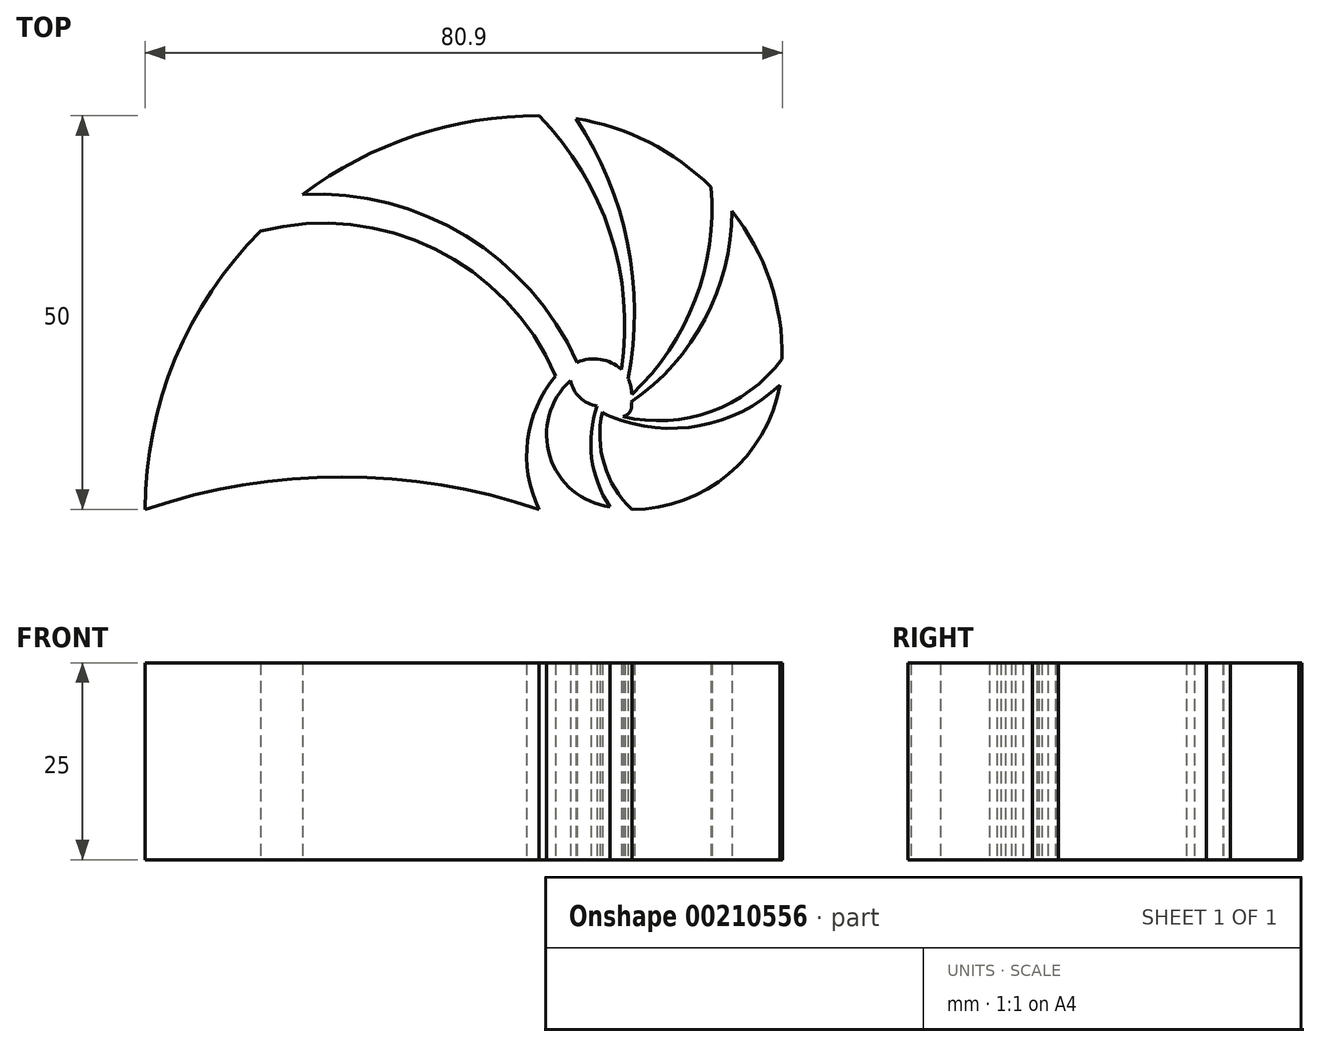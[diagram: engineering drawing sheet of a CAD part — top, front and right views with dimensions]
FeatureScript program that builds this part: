
annotation { "Feature Type Name" : "Feature", "Feature Type Description" : "" }
export const myFeature = defineFeature(function(context is Context, id is Id, definition is map)
    precondition{}
    {
        {
            var Q0;
            Q0=qCreatedBy(makeId("Top.planeOp"),FACE);
            var sketch = newSketch(context, id + "F0", { "sketchPlane" : qUnion([Q0])});
            skPoint(sketch, "E0", {"position": v(4.04, -30.8) * mm});
            skArc(sketch, "E1", {"start": v(-45.96, -30.8) * mm, "mid": v(-31.32, 4.55) * mm, "end": v(4.04, 19.2) * mm, "construction": true});
            skArc(sketch, "E2.MirrorCS", {"start": v(4.04, 19.2) * mm, "mid": v(25.89, 10.14) * mm, "end": v(34.94, -11.7) * mm, "construction": true});
            skArc(sketch, "E3.MirrorCS", {"start": v(34.94, -11.7) * mm, "mid": v(29.34, -25.21) * mm, "end": v(15.84, -30.8) * mm, "construction": true});
            skArc(sketch, "E4.MirrorCS", {"start": v(15.84, -30.8) * mm, "mid": v(7.5, -27.35) * mm, "end": v(4.05, -19) * mm, "construction": true});
            skArc(sketch, "E5.MirrorCS", {"start": v(4.04, -19) * mm, "mid": v(6.17, -13.85) * mm, "end": v(11.34, -11.7) * mm, "construction": true});
            skArc(sketch, "E6.MirrorCS", {"start": v(11.34, -11.7) * mm, "mid": v(14.52, -13.03) * mm, "end": v(15.84, -16.2) * mm, "construction": true});
            skPoint(sketch, "E7", {"position": v(-31.32, 4.55) * mm});
            skPoint(sketch, "E8", {"position": v(25.89, 10.14) * mm});
            skPoint(sketch, "E9", {"position": v(29.34, -25.21) * mm});
            skPoint(sketch, "E10", {"position": v(7.5, -27.35) * mm});
            skPoint(sketch, "E11", {"position": v(6.17, -13.85) * mm});
            skPoint(sketch, "E12", {"position": v(14.52, -13.03) * mm});
            skArc(sketch, "E13", {"start": v(-31.32, 4.55) * mm, "mid": v(-42.16, -11.67) * mm, "end": v(-45.96, -30.8) * mm});
            skArc(sketch, "E14", {"start": v(4.04, -30.8) * mm, "mid": v(-20.96, -26.69) * mm, "end": v(-45.96, -30.8) * mm});
            skArc(sketch, "E15", {"start": v(6.17, -13.85) * mm, "mid": v(-9.18, 2.27) * mm, "end": v(-31.32, 4.55) * mm});
            skArc(sketch, "E16", {"start": v(6.17, -13.85) * mm, "mid": v(2.6, -22.01) * mm, "end": v(4.04, -30.8) * mm});
            skArc(sketch, "E17", {"start": v(4.04, 19.2) * mm, "mid": v(-11.79, 16.67) * mm, "end": v(-25.96, 9.2) * mm});
            skArc(sketch, "E18", {"start": v(14.52, -13.03) * mm, "mid": v(11.83, -11.76) * mm, "end": v(8.88, -12.13) * mm});
            skArc(sketch, "E19", {"start": v(8.88, -12.13) * mm, "mid": v(-5.25, 3.9) * mm, "end": v(-25.96, 9.2) * mm});
            skArc(sketch, "E20", {"start": v(14.52, -13.03) * mm, "mid": v(13.08, 4.32) * mm, "end": v(4.04, 19.2) * mm});
            skArc(sketch, "E21", {"start": v(25.89, 10.14) * mm, "mid": v(18, 15.85) * mm, "end": v(8.73, 18.83) * mm});
            skArc(sketch, "E22", {"start": v(15.37, -14.22) * mm, "mid": v(15.3, 2.96) * mm, "end": v(8.73, 18.83) * mm});
            skArc(sketch, "E23", {"start": v(15.84, -16.2) * mm, "mid": v(23.88, -4.19) * mm, "end": v(25.89, 10.14) * mm});
            skArc(sketch, "E24", {"start": v(15.84, -16.2) * mm, "mid": v(15.7, -15.19) * mm, "end": v(15.37, -14.22) * mm});
            skArc(sketch, "E25", {"start": v(34.94, -11.7) * mm, "mid": v(33.39, -1.77) * mm, "end": v(28.58, 7.07) * mm});
            skArc(sketch, "E26", {"start": v(14.71, -19.02) * mm, "mid": v(15.64, -18.33) * mm, "end": v(15.75, -17.17) * mm});
            skArc(sketch, "E27", {"start": v(15.75, -17.17) * mm, "mid": v(25.13, -6.62) * mm, "end": v(28.58, 7.07) * mm});
            skArc(sketch, "E28", {"start": v(14.71, -19.02) * mm, "mid": v(25.91, -18.38) * mm, "end": v(34.94, -11.7) * mm});
            skArc(sketch, "E29", {"start": v(15.84, -30.8) * mm, "mid": v(28.12, -26.33) * mm, "end": v(34.65, -15) * mm});
            skArc(sketch, "E30", {"start": v(12.09, -18.43) * mm, "mid": v(12.59, -18.78) * mm, "end": v(13.14, -19.02) * mm});
            skArc(sketch, "E31", {"start": v(12.09, -18.43) * mm, "mid": v(12.34, -25.11) * mm, "end": v(15.84, -30.8) * mm});
            skArc(sketch, "E32", {"start": v(13.14, -19.02) * mm, "mid": v(24.48, -20.17) * mm, "end": v(34.65, -15) * mm});
            skArc(sketch, "E33", {"start": v(8.04, -14.45) * mm, "mid": v(5.43, -24.07) * mm, "end": v(13.06, -30.48) * mm});
            skArc(sketch, "E34", {"start": v(8.04, -14.45) * mm, "mid": v(9.24, -16.6) * mm, "end": v(11.44, -17.67) * mm});
            skArc(sketch, "E35", {"start": v(11.44, -17.67) * mm, "mid": v(10.74, -24.27) * mm, "end": v(13.06, -30.48) * mm});
            skSolve(sketch);
        }
        {
            var Q0;
            Q0 = qSketchRegion(id + "F0", true);
            extrude(context, id + "F1", {"entities" : qUnion([Q0]), "depth" : 25 * mm});
        }
    });
